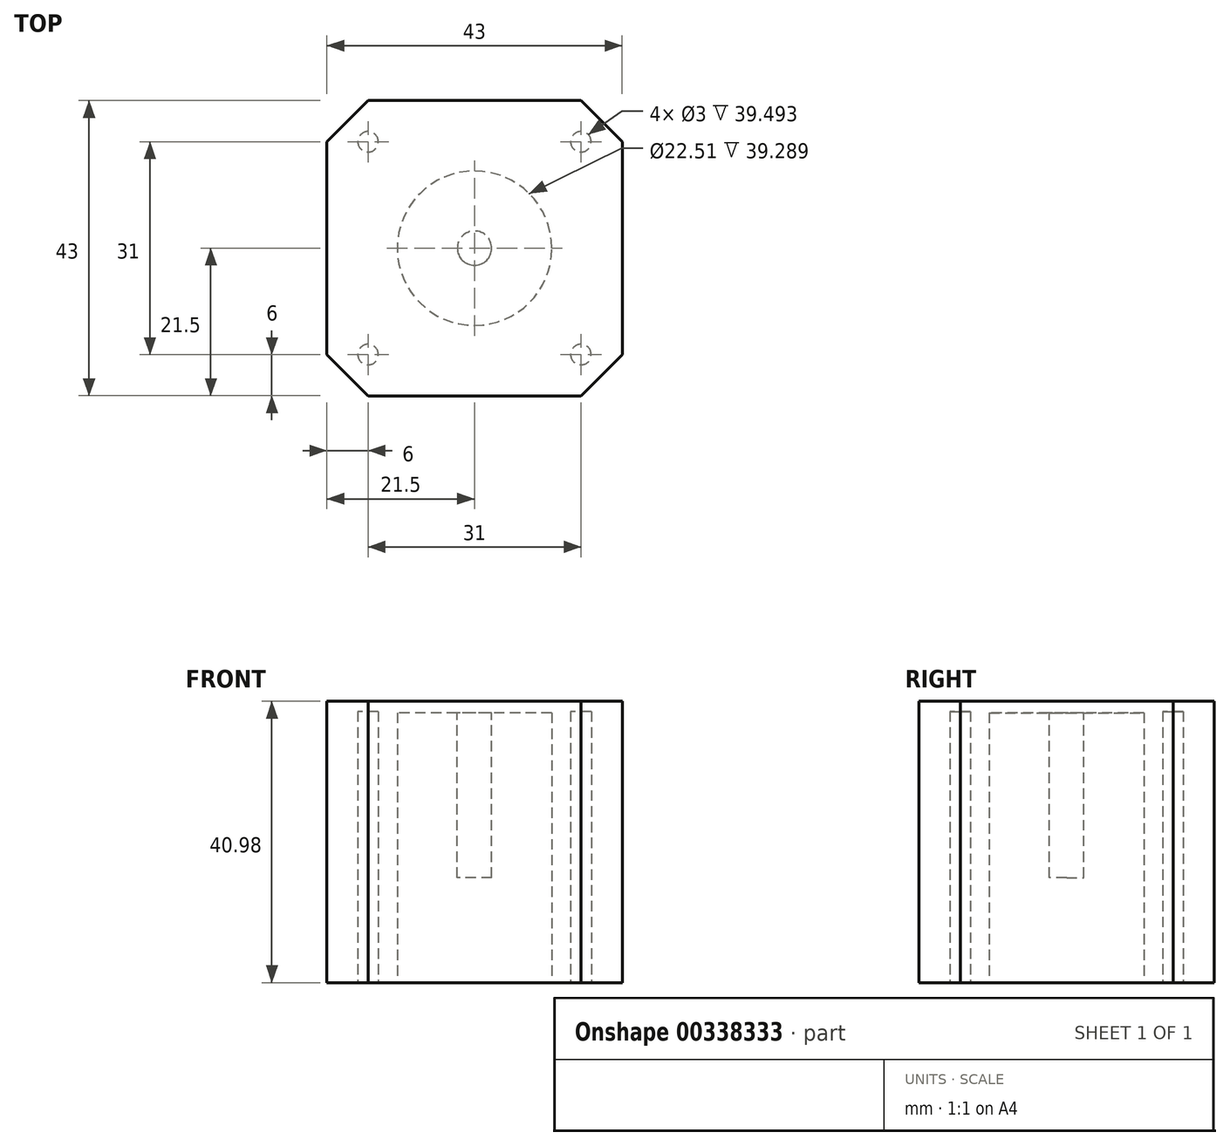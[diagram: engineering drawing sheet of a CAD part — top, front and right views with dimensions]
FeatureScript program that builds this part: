
annotation { "Feature Type Name" : "Feature", "Feature Type Description" : "" }
export const myFeature = defineFeature(function(context is Context, id is Id, definition is map)
    precondition{}
    {
        {
            var Q0;
            Q0=qCreatedBy(makeId("Top.planeOp"),FACE);
            var sketch = newSketch(context, id + "F0", { "sketchPlane" : qUnion([Q0])});
            skCircle(sketch, "E0", {"center": v(0, 0) * mm, "radius": 11.25 * mm});
            skLineSegment(sketch, "E1.bottom", {"start": v(15.5, -15.5) * mm, "end": v(-15.5, -15.5) * mm, "construction": true});
            skLineSegment(sketch, "E1.top", {"start": v(15.5, 15.5) * mm, "end": v(-15.5, 15.5) * mm, "construction": true});
            skLineSegment(sketch, "E1.left", {"start": v(15.5, -15.5) * mm, "end": v(15.5, 15.5) * mm, "construction": true});
            skLineSegment(sketch, "E1.right", {"start": v(-15.5, -15.5) * mm, "end": v(-15.5, 15.5) * mm, "construction": true});
            skCircle(sketch, "E2", {"center": v(15.5, -15.5) * mm, "radius": 1.5 * mm});
            skCircle(sketch, "E3", {"center": v(15.5, 15.5) * mm, "radius": 1.5 * mm});
            skCircle(sketch, "E4", {"center": v(-15.5, 15.5) * mm, "radius": 1.5 * mm});
            skCircle(sketch, "E5", {"center": v(-15.5, -15.5) * mm, "radius": 1.5 * mm});
            skLineSegment(sketch, "E6", {"start": v(0, 0) * mm, "end": v(0, 21.5) * mm, "construction": true});
            skLineSegment(sketch, "E7", {"start": v(-21.5, 21.5) * mm, "end": v(21.5, 21.5) * mm});
            skLineSegment(sketch, "E8", {"start": v(21.5, 21.5) * mm, "end": v(21.5, -21.5) * mm});
            skLineSegment(sketch, "E9", {"start": v(21.5, -21.5) * mm, "end": v(-21.5, -21.5) * mm});
            skLineSegment(sketch, "E10", {"start": v(-21.5, 21.5) * mm, "end": v(-21.5, -21.5) * mm});
            skSolve(sketch);
        }
        {
            var Q0;
            Q0=qSketchRegion(id+"F0",true);
            extrude(context, id + "F1", {"entities" : qUnion([Q0]), "depth" : 40.98 * mm});
        }
        {
            var Q0;
            Q0=makeQuery(id+"F1.opExtrude","SWEPT_EDGE",EDGE,{"disambiguationData":[OSD([sQuery(id+"F0.wireOp",EDGE,"E8"),sQuery(id+"F0.wireOp",EDGE,"E9")])]});
            var Q1;
            Q1=makeQuery(id+"F1.opExtrude","SWEPT_EDGE",EDGE,{"disambiguationData":[OSD([sQuery(id+"F0.wireOp",EDGE,"E7"),sQuery(id+"F0.wireOp",EDGE,"E8")])]});
            var Q2;
            Q2=makeQuery(id+"F1.opExtrude","SWEPT_EDGE",EDGE,{"disambiguationData":[OSD([sQuery(id+"F0.wireOp",EDGE,"E7"),sQuery(id+"F0.wireOp",EDGE,"E10")])]});
            var Q3;
            Q3=makeQuery(id+"F1.opExtrude","SWEPT_EDGE",EDGE,{"disambiguationData":[OSD([sQuery(id+"F0.wireOp",EDGE,"E10"),sQuery(id+"F0.wireOp",EDGE,"RUztX63a-jUML-vWRW-I2LU-GtVIhsBZly2z")])]});
            chamfer(context, id + "F2", {"entities" : qUnion([Q0, Q1, Q2, Q3]), "width" : 6 * mm, "tangentPropagation" : true});
        }
        {
            var Q0;
            Q0=makeQuery(id+"F1.opExtrude","CAP_FACE",FACE,{"disambiguationData":[OSD([sQuery(id+"F0.wireOp",EDGE,"E0"),sQuery(id+"F0.wireOp",EDGE,"E2"),sQuery(id+"F0.wireOp",EDGE,"E3"),sQuery(id+"F0.wireOp",EDGE,"E4"),sQuery(id+"F0.wireOp",EDGE,"E5"),sQuery(id+"F0.wireOp",EDGE,"E7"),sQuery(id+"F0.wireOp",EDGE,"E8"),sQuery(id+"F0.wireOp",EDGE,"E9"),sQuery(id+"F0.wireOp",EDGE,"E10")])],"isStart":false});
            var sketch = newSketch(context, id + "F3", { "sketchPlane" : qUnion([Q0])});
            skLineSegment(sketch, "E11.bottom", {"start": v(-17, -17) * mm, "end": v(17, -17) * mm});
            skLineSegment(sketch, "E11.top", {"start": v(-17, 17) * mm, "end": v(17, 17) * mm});
            skLineSegment(sketch, "E11.left", {"start": v(-17, -17) * mm, "end": v(-17, 17) * mm});
            skLineSegment(sketch, "E11.right", {"start": v(17, -17) * mm, "end": v(17, 17) * mm});
            skPoint(sketch, "E11.middle", {"position": v(0, 0) * mm});
            skSolve(sketch);
        }
        {
            var Q0;
            Q0 = qSketchRegion(id + "F3", true);
            extrude(context, id + "F4", {"entities" : qUnion([Q0]), "operationType" : NewBodyOperationType.ADD, "oppositeDirection" : true, "depth" : (1.61 - (1 / 8)) * mm});
        }
        {
            var Q0;
            Q0=makeQuery(id+"F4.boolean.opBoolean","SPLIT",FACE,{"disambiguationData":[TD([makeQuery(id+"F1.opExtrude","SWEPT_FACE",FACE,{"disambiguationData":[OSD([sQuery(id+"F0.wireOp",EDGE,"E0")])]})])],"derivedFrom":makeQuery(id+"F4.opExtrude","CAP_FACE",FACE,{"disambiguationData":[OSD([sQuery(id+"F3.wireOp",EDGE,"E11.bottom"),sQuery(id+"F3.wireOp",EDGE,"E11.top"),sQuery(id+"F3.wireOp",EDGE,"E11.left"),sQuery(id+"F3.wireOp",EDGE,"E11.right")])],"isStart":false})});
            extrude(context, id + "F5", {"entities" : qUnion([Q0]), "operationType" : NewBodyOperationType.ADD, "depth" : (0.08 + (1 / 8)) * mm});
        }
        {
            var Q0;
            Q0=makeQuery(id+"F5.opExtrude","CAP_FACE",FACE,{"disambiguationData":[OSD([sQuery(id+"F3.wireOp",EDGE,"E11.bottom"),sQuery(id+"F3.wireOp",EDGE,"E11.top"),sQuery(id+"F3.wireOp",EDGE,"E11.left"),sQuery(id+"F3.wireOp",EDGE,"E11.right")])],"isStart":false});
            var sketch = newSketch(context, id + "F6", { "sketchPlane" : qUnion([Q0])});
            skCircle(sketch, "E12", {"center": v(0, 0) * mm, "radius": 2.5 * mm});
            skSolve(sketch);
        }
        {
            var Q0;
            Q0 = qSketchRegion(id + "F6", true);
            extrude(context, id + "F7", {"entities" : qUnion([Q0]), "operationType" : NewBodyOperationType.ADD, "depth" : 24 * mm});
        }
    });
